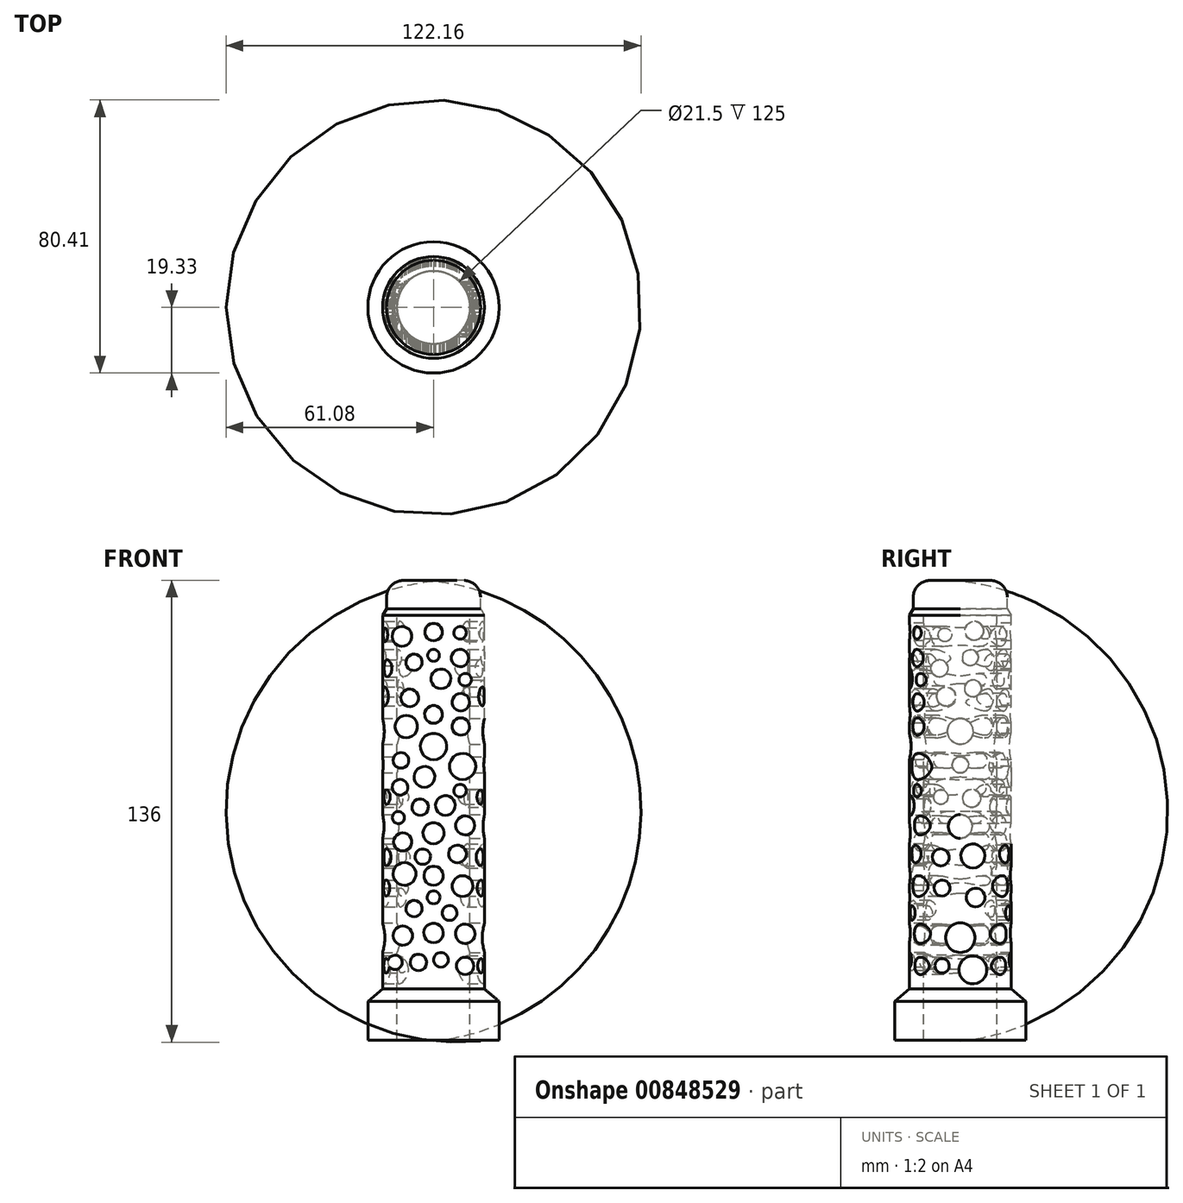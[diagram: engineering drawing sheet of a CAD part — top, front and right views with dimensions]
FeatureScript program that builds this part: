
annotation { "Feature Type Name" : "Feature", "Feature Type Description" : "" }
export const myFeature = defineFeature(function(context is Context, id is Id, definition is map)
    precondition{}
    {
        {
            var Q0;
            Q0=qCreatedBy(makeId("Front.planeOp"),FACE);
            var sketch = newSketch(context, id + "F0", { "sketchPlane" : qUnion([Q0])});
            skLineSegment(sketch, "E0", {"start": v(0, 136.76) * mm, "end": v(0, -87.15) * mm, "construction": true});
            skLineSegment(sketch, "E1", {"start": v(15, 25.96) * mm, "end": v(19.33, 22.34) * mm});
            skLineSegment(sketch, "E2", {"start": v(19.33, 22.34) * mm, "end": v(19.33, 10.96) * mm});
            skLineSegment(sketch, "E3", {"start": v(19.33, 10.96) * mm, "end": v(10.75, 10.96) * mm});
            skLineSegment(sketch, "E4", {"start": v(10.75, 10.96) * mm, "end": v(10.75, 135.96) * mm});
            skLineSegment(sketch, "E5", {"start": v(10.75, 135.96) * mm, "end": v(0, 135.96) * mm});
            skLineSegment(sketch, "E6", {"start": v(0, 135.96) * mm, "end": v(0, 145.96) * mm});
            skLineSegment(sketch, "E7", {"start": v(13.85, 145.96) * mm, "end": v(13.85, 137.96) * mm});
            skLineSegment(sketch, "E8", {"start": v(13.85, 137.96) * mm, "end": v(15, 135.96) * mm});
            skLineSegment(sketch, "E9", {"start": v(15, 135.96) * mm, "end": v(15, 25.96) * mm});
            skArc(sketch, "E10", {"start": v(13.85, 145.96) * mm, "mid": v(6.92, 146.32) * mm, "end": v(0, 145.96) * mm});
            skSolve(sketch);
        }
        {
            var Q0;
            Q0 = qSketchRegion(id + "F0", true);
            var Q1;
            Q1=sQuery(id+"F0.wireOp",EDGE,"E0");
            revolve(context, id + "F1", {"surfaceOperationType" : NewSurfaceOperationType.NEW, "entities" : qUnion([Q0]), "axis" : qUnion([Q1]), "revolveType" : RevolveType.FULL});
        }
        {
            var Q0;
            Q0=qCreatedBy(makeId("Front.planeOp"),FACE);
            var sketch = newSketch(context, id + "F2", { "sketchPlane" : qUnion([Q0])});
            skCircle(sketch, "E11", {"center": v(-11.35, 33.8) * mm, "radius": 2.1 * mm});
            skCircle(sketch, "E12", {"center": v(-4.46, 33.8) * mm, "radius": 2.42 * mm});
            skCircle(sketch, "E13", {"center": v(2.18, 34.57) * mm, "radius": 2.17 * mm});
            skCircle(sketch, "E14", {"center": v(9.33, 32.78) * mm, "radius": 2.55 * mm});
            skCircle(sketch, "E15", {"center": v(0, 131.08) * mm, "radius": 2.57 * mm});
            skCircle(sketch, "E16", {"center": v(7.8, 130.83) * mm, "radius": 1.86 * mm});
            skCircle(sketch, "E17", {"center": v(-9.31, 129.8) * mm, "radius": 2.91 * mm});
            skCircle(sketch, "E18", {"center": v(-5.74, 122.15) * mm, "radius": 2.4 * mm});
            skCircle(sketch, "E19", {"center": v(0, 124.2) * mm, "radius": 1.74 * mm});
            skCircle(sketch, "E20", {"center": v(7.8, 123.43) * mm, "radius": 2.55 * mm});
            skCircle(sketch, "E21", {"center": v(2.18, 117.3) * mm, "radius": 2.91 * mm});
            skCircle(sketch, "E22", {"center": v(-7.01, 111.68) * mm, "radius": 2.6 * mm});
            skCircle(sketch, "E23", {"center": v(9.33, 117.04) * mm, "radius": 1.86 * mm});
            skCircle(sketch, "E24", {"center": v(8.05, 110.4) * mm, "radius": 2.57 * mm});
            skCircle(sketch, "E25", {"center": v(0, 106.83) * mm, "radius": 2.63 * mm});
            skCircle(sketch, "E26", {"center": v(8.05, 103.25) * mm, "radius": 2.57 * mm});
            skCircle(sketch, "E27", {"center": v(-8.03, 103.25) * mm, "radius": 3.32 * mm});
            skCircle(sketch, "E28", {"center": v(0, 97.38) * mm, "radius": 3.88 * mm});
            skCircle(sketch, "E29", {"center": v(8.56, 91.5) * mm, "radius": 3.86 * mm});
            skCircle(sketch, "E30", {"center": v(-9.57, 93.3) * mm, "radius": 2.31 * mm});
            skCircle(sketch, "E31", {"center": v(-2.67, 88.45) * mm, "radius": 3.06 * mm});
            skCircle(sketch, "E32", {"center": v(-9.82, 85.38) * mm, "radius": 2.31 * mm});
            skCircle(sketch, "E33", {"center": v(3.46, 80.02) * mm, "radius": 2.91 * mm});
            skCircle(sketch, "E34", {"center": v(7.8, 84.36) * mm, "radius": 1.86 * mm});
            skCircle(sketch, "E35", {"center": v(-3.95, 79.5) * mm, "radius": 2.42 * mm});
            skCircle(sketch, "E36", {"center": v(-10.33, 76.45) * mm, "radius": 1.79 * mm});
            skCircle(sketch, "E37", {"center": v(0, 71.85) * mm, "radius": 3.1 * mm});
            skCircle(sketch, "E38", {"center": v(9.33, 74.15) * mm, "radius": 2.8 * mm});
            skCircle(sketch, "E39", {"center": v(7.03, 65.72) * mm, "radius": 2.6 * mm});
            skCircle(sketch, "E40", {"center": v(-3.18, 64.96) * mm, "radius": 2.28 * mm});
            skCircle(sketch, "E41", {"center": v(-9.06, 69.3) * mm, "radius": 2.67 * mm});
            skCircle(sketch, "E42", {"center": v(-8.55, 59.85) * mm, "radius": 3.36 * mm});
            skCircle(sketch, "E43", {"center": v(0, 59.34) * mm, "radius": 2.84 * mm});
            skCircle(sketch, "E44", {"center": v(8.56, 56.27) * mm, "radius": 3.07 * mm});
            skCircle(sketch, "E45", {"center": v(0, 52.96) * mm, "radius": 1.9 * mm});
            skCircle(sketch, "E46", {"center": v(-5.74, 49.64) * mm, "radius": 2.4 * mm});
            skCircle(sketch, "E47", {"center": v(9.33, 42.23) * mm, "radius": 2.85 * mm});
            skCircle(sketch, "E48", {"center": v(0, 42.49) * mm, "radius": 2.88 * mm});
            skCircle(sketch, "E49", {"center": v(-9.06, 41.72) * mm, "radius": 2.85 * mm});
            skCircle(sketch, "E50", {"center": v(4.73, 48.36) * mm, "radius": 2.18 * mm});
            skSolve(sketch);
        }
        {
            var Q0;
            Q0 = qSketchRegion(id + "F2", true);
            extrude(context, id + "F3", {"entities" : qUnion([Q0]), "operationType" : NewBodyOperationType.REMOVE, "endBound" : BoundingType.SYMMETRIC, "oppositeDirection" : true, "depth" : 100 * mm, "offsetDistance" : 25 * mm});
        }
        {
            var Q0;
            Q0=qCreatedBy(makeId("Right.planeOp"),FACE);
            var sketch = newSketch(context, id + "F4", { "sketchPlane" : qUnion([Q0])});
            skCircle(sketch, "E51", {"center": v(-4.57, 130.25) * mm, "radius": 2.01 * mm});
            skCircle(sketch, "E52", {"center": v(4.11, 131.43) * mm, "radius": 2.76 * mm});
            skCircle(sketch, "E53", {"center": v(2.93, 123.54) * mm, "radius": 2.37 * mm});
            skCircle(sketch, "E54", {"center": v(-6.14, 120.39) * mm, "radius": 2.5 * mm});
            skCircle(sketch, "E55", {"center": v(3.72, 114.47) * mm, "radius": 2.5 * mm});
            skCircle(sketch, "E56", {"center": v(-4.17, 112.1) * mm, "radius": 2.79 * mm});
            skCircle(sketch, "E57", {"center": v(0, 101.85) * mm, "radius": 3.8 * mm});
            skCircle(sketch, "E58", {"center": v(0, 41.09) * mm, "radius": 4.34 * mm});
            skCircle(sketch, "E59", {"center": v(4.5, 52.92) * mm, "radius": 2.76 * mm});
            skCircle(sketch, "E60", {"center": v(0, 91.98) * mm, "radius": 2.38 * mm});
            skCircle(sketch, "E61", {"center": v(-5.75, 82.51) * mm, "radius": 2.12 * mm});
            skCircle(sketch, "E62", {"center": v(3.32, 82.12) * mm, "radius": 2.65 * mm});
            skCircle(sketch, "E63", {"center": v(0, 73.83) * mm, "radius": 3.51 * mm});
            skCircle(sketch, "E64", {"center": v(3.72, 65.15) * mm, "radius": 3.55 * mm});
            skCircle(sketch, "E65", {"center": v(-5.75, 64.76) * mm, "radius": 2.5 * mm});
            skCircle(sketch, "E66", {"center": v(-5.35, 55.69) * mm, "radius": 2.37 * mm});
            skCircle(sketch, "E67", {"center": v(3.72, 31.62) * mm, "radius": 4.12 * mm});
            skCircle(sketch, "E68", {"center": v(-5.35, 32.8) * mm, "radius": 2.12 * mm});
            skSolve(sketch);
        }
        {
            var Q0;
            Q0 = qSketchRegion(id + "F4", true);
            extrude(context, id + "F5", {"entities" : qUnion([Q0]), "operationType" : NewBodyOperationType.REMOVE, "endBound" : BoundingType.SYMMETRIC, "oppositeDirection" : true, "depth" : 100 * mm, "offsetDistance" : 25 * mm});
        }
        {
            var Q0;
            Q0=makeQuery(id+"F1.opRevolve","SWEPT_EDGE",EDGE,{"disambiguationData":[OSD([sQuery(id+"F0.wireOp",EDGE,"E7"),sQuery(id+"F0.wireOp",EDGE,"E10")])]});
            fillet(context, id + "F6", {"entities" : qUnion([Q0]), "radius" : 5 * mm, "tangentPropagation" : true, "allowEdgeOverflow" : false});
        }
    });
